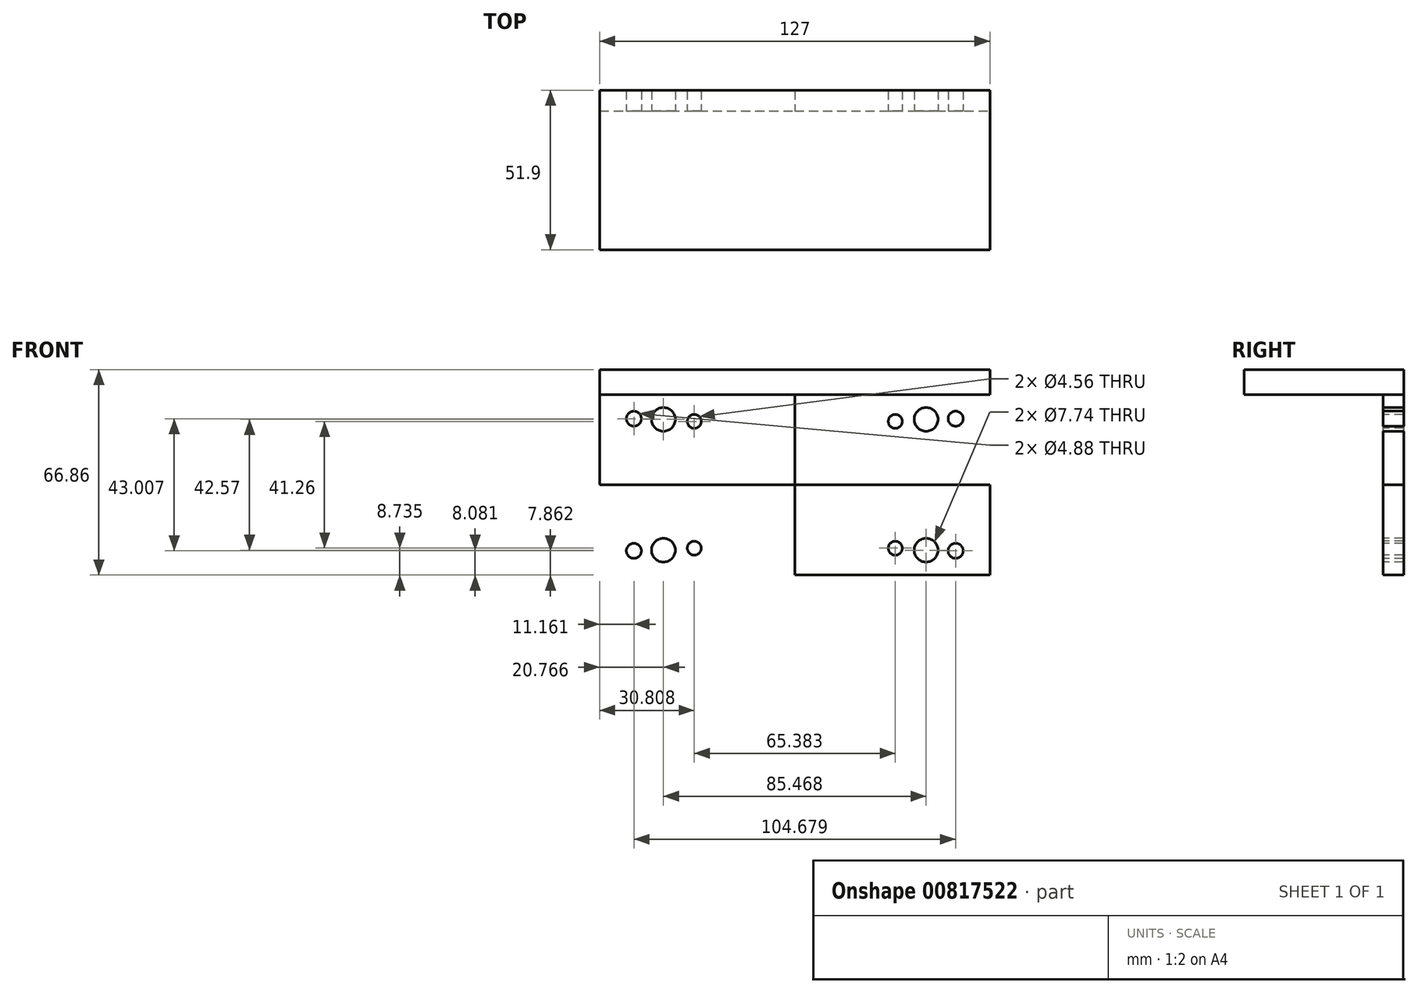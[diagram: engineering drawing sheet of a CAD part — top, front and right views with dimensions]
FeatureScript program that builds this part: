
annotation { "Feature Type Name" : "Feature", "Feature Type Description" : "" }
export const myFeature = defineFeature(function(context is Context, id is Id, definition is map)
    precondition{}
    {
        {
            var Q0;
            Q0=qCreatedBy(makeId("Right.planeOp"),FACE);
            var sketch = newSketch(context, id + "F0", { "sketchPlane" : qUnion([Q0])});
            skLineSegment(sketch, "E0", {"start": v(-51.9, 0) * mm, "end": v(0, 0) * mm});
            skLineSegment(sketch, "E1", {"start": v(0, 0) * mm, "end": v(0, -66.86) * mm});
            skLineSegment(sketch, "E2", {"start": v(0, -66.86) * mm, "end": v(-6.71, -66.86) * mm});
            skLineSegment(sketch, "E3", {"start": v(-6.71, -66.86) * mm, "end": v(-6.71, -8.13) * mm});
            skLineSegment(sketch, "E4", {"start": v(-6.71, -8.13) * mm, "end": v(-51.9, -8.13) * mm});
            skLineSegment(sketch, "E5", {"start": v(-51.9, -8.13) * mm, "end": v(-51.9, 0) * mm});
            skSolve(sketch);
        }
        {
            var Q0;
            Q0=makeQuery(id+"F0.imprint","IMPRINT",FACE,{"disambiguationData":[TD([[makeQuery(id+"F0.imprint","IMPRINT",EDGE,{"derivedFrom":sQuery(id+"F0.wireOp",EDGE,"E0")}),-1.0]])]});
            extrude(context, id + "F1", {"entities" : qUnion([Q0]), "depth" : 63.5 * mm, "offsetDistance" : 25.4 * mm});
        }
        {
            var Q0;
            Q0=makeQuery(id+"F1.opExtrude","CAP_FACE",FACE,{"disambiguationData":[OSD([sQuery(id+"F0.wireOp",EDGE,"E0"),sQuery(id+"F0.wireOp",EDGE,"E1"),sQuery(id+"F0.wireOp",EDGE,"E2"),sQuery(id+"F0.wireOp",EDGE,"E3"),sQuery(id+"F0.wireOp",EDGE,"E4"),sQuery(id+"F0.wireOp",EDGE,"E5")])],"isStart":true});
            extrude(context, id + "F2", {"entities" : qUnion([Q0]), "operationType" : NewBodyOperationType.ADD, "depth" : 63.5 * mm, "offsetDistance" : 25.4 * mm});
        }
        {
            var Q0;
            {var subQ0=sQuery(id+"F0.wireOp",EDGE,"E3");Q0=makeQuery(id+"F2.boolean.opBoolean","MERGE",FACE,{"derivedFrom":[makeQuery(id+"F1.opExtrude","SWEPT_FACE",FACE,{"disambiguationData":[OSD([subQ0])]}),makeQuery(id+"F2.opExtrude","SWEPT_FACE",FACE,{"disambiguationData":[OSD([subQ0])]})]});}
            var sketch = newSketch(context, id + "F3", { "sketchPlane" : qUnion([Q0])});
            skLineSegment(sketch, "E6", {"start": v(0, 0) * mm, "end": v(0, -66.86) * mm});
            skCircle(sketch, "E7", {"center": v(-52.34, -16) * mm, "radius": 2.44 * mm});
            skCircle(sketch, "E8", {"center": v(-42.73, -16.2) * mm, "radius": 3.87 * mm});
            skCircle(sketch, "E9", {"center": v(-32.7, -16.86) * mm, "radius": 2.28 * mm});
            skLineSegment(sketch, "E10", {"start": v(-63.5, -37.5) * mm, "end": v(63.5, -37.5) * mm});
            skCircle(sketch, "E11.MirrorC", {"center": v(-42.73, -58.78) * mm, "radius": 3.87 * mm});
            skCircle(sketch, "E12.MirrorC", {"center": v(-52.34, -59) * mm, "radius": 2.44 * mm});
            skCircle(sketch, "E13.MirrorC", {"center": v(-32.7, -58.12) * mm, "radius": 2.28 * mm});
            skCircle(sketch, "E14.MirrorC", {"center": v(32.7, -16.86) * mm, "radius": 2.28 * mm});
            skCircle(sketch, "E15.MirrorC", {"center": v(42.73, -16.2) * mm, "radius": 3.87 * mm});
            skCircle(sketch, "E16.MirrorC", {"center": v(52.34, -16) * mm, "radius": 2.44 * mm});
            skCircle(sketch, "E17.MirrorC", {"center": v(32.7, -58.12) * mm, "radius": 2.28 * mm});
            skCircle(sketch, "E18.MirrorC", {"center": v(42.73, -58.78) * mm, "radius": 3.87 * mm});
            skCircle(sketch, "E19.MirrorC", {"center": v(52.34, -59) * mm, "radius": 2.44 * mm});
            skSolve(sketch);
        }
        {
            var Q0;
            Q0=makeQuery(id+"F3.imprint","IMPRINT",FACE,{"disambiguationData":[TD([[makeQuery(id+"F3.imprint","IMPRINT",EDGE,{"derivedFrom":sQuery(id+"F3.wireOp",EDGE,"E7")}),1.0]])]});
            var Q1;
            Q1=makeQuery(id+"F3.imprint","IMPRINT",FACE,{"disambiguationData":[TD([[makeQuery(id+"F3.imprint","IMPRINT",EDGE,{"derivedFrom":sQuery(id+"F3.wireOp",EDGE,"E8")}),1.0]])]});
            var Q2;
            Q2=makeQuery(id+"F3.imprint","IMPRINT",FACE,{"disambiguationData":[TD([[makeQuery(id+"F3.imprint","IMPRINT",EDGE,{"derivedFrom":sQuery(id+"F3.wireOp",EDGE,"E9")}),1.0]])]});
            var Q3;
            Q3=makeQuery(id+"F3.imprint","IMPRINT",FACE,{"disambiguationData":[TD([[makeQuery(id+"F3.imprint","IMPRINT",EDGE,{"derivedFrom":sQuery(id+"F3.wireOp",EDGE,"E14.MirrorC")}),-1.0]])]});
            var Q4;
            Q4=makeQuery(id+"F3.imprint","IMPRINT",FACE,{"disambiguationData":[TD([[makeQuery(id+"F3.imprint","IMPRINT",EDGE,{"derivedFrom":sQuery(id+"F3.wireOp",EDGE,"E15.MirrorC")}),-1.0]])]});
            var Q5;
            Q5=makeQuery(id+"F3.imprint","IMPRINT",FACE,{"disambiguationData":[TD([[makeQuery(id+"F3.imprint","IMPRINT",EDGE,{"derivedFrom":sQuery(id+"F3.wireOp",EDGE,"E16.MirrorC")}),-1.0]])]});
            var Q6;
            Q6=makeQuery(id+"F3.imprint","IMPRINT",FACE,{"disambiguationData":[TD([[makeQuery(id+"F3.imprint","IMPRINT",EDGE,{"derivedFrom":sQuery(id+"F3.wireOp",EDGE,"E19.MirrorC")}),1.0]])]});
            var Q7;
            Q7=makeQuery(id+"F3.imprint","IMPRINT",FACE,{"disambiguationData":[TD([[makeQuery(id+"F3.imprint","IMPRINT",EDGE,{"derivedFrom":sQuery(id+"F3.wireOp",EDGE,"E18.MirrorC")}),1.0]])]});
            var Q8;
            Q8=makeQuery(id+"F3.imprint","IMPRINT",FACE,{"disambiguationData":[TD([[makeQuery(id+"F3.imprint","IMPRINT",EDGE,{"derivedFrom":sQuery(id+"F3.wireOp",EDGE,"E17.MirrorC")}),1.0]])]});
            var Q9;
            Q9=makeQuery(id+"F3.imprint","IMPRINT",FACE,{"disambiguationData":[TD([[makeQuery(id+"F3.imprint","IMPRINT",EDGE,{"derivedFrom":sQuery(id+"F3.wireOp",EDGE,"E12.MirrorC")}),-1.0]])]});
            var Q10;
            Q10=makeQuery(id+"F3.imprint","IMPRINT",FACE,{"disambiguationData":[TD([[makeQuery(id+"F3.imprint","IMPRINT",EDGE,{"derivedFrom":sQuery(id+"F3.wireOp",EDGE,"E11.MirrorC")}),-1.0]])]});
            var Q11;
            Q11=makeQuery(id+"F3.imprint","IMPRINT",FACE,{"disambiguationData":[TD([[makeQuery(id+"F3.imprint","IMPRINT",EDGE,{"derivedFrom":sQuery(id+"F3.wireOp",EDGE,"E13.MirrorC")}),-1.0]])]});
            extrude(context, id + "F4", {"entities" : qUnion([Q0, Q1, Q2, Q3, Q4, Q5, Q6, Q7, Q8, Q9, Q10, Q11]), "operationType" : NewBodyOperationType.REMOVE, "oppositeDirection" : true, "depth" : 25.4 * mm, "offsetDistance" : 25.4 * mm});
        }
    });
